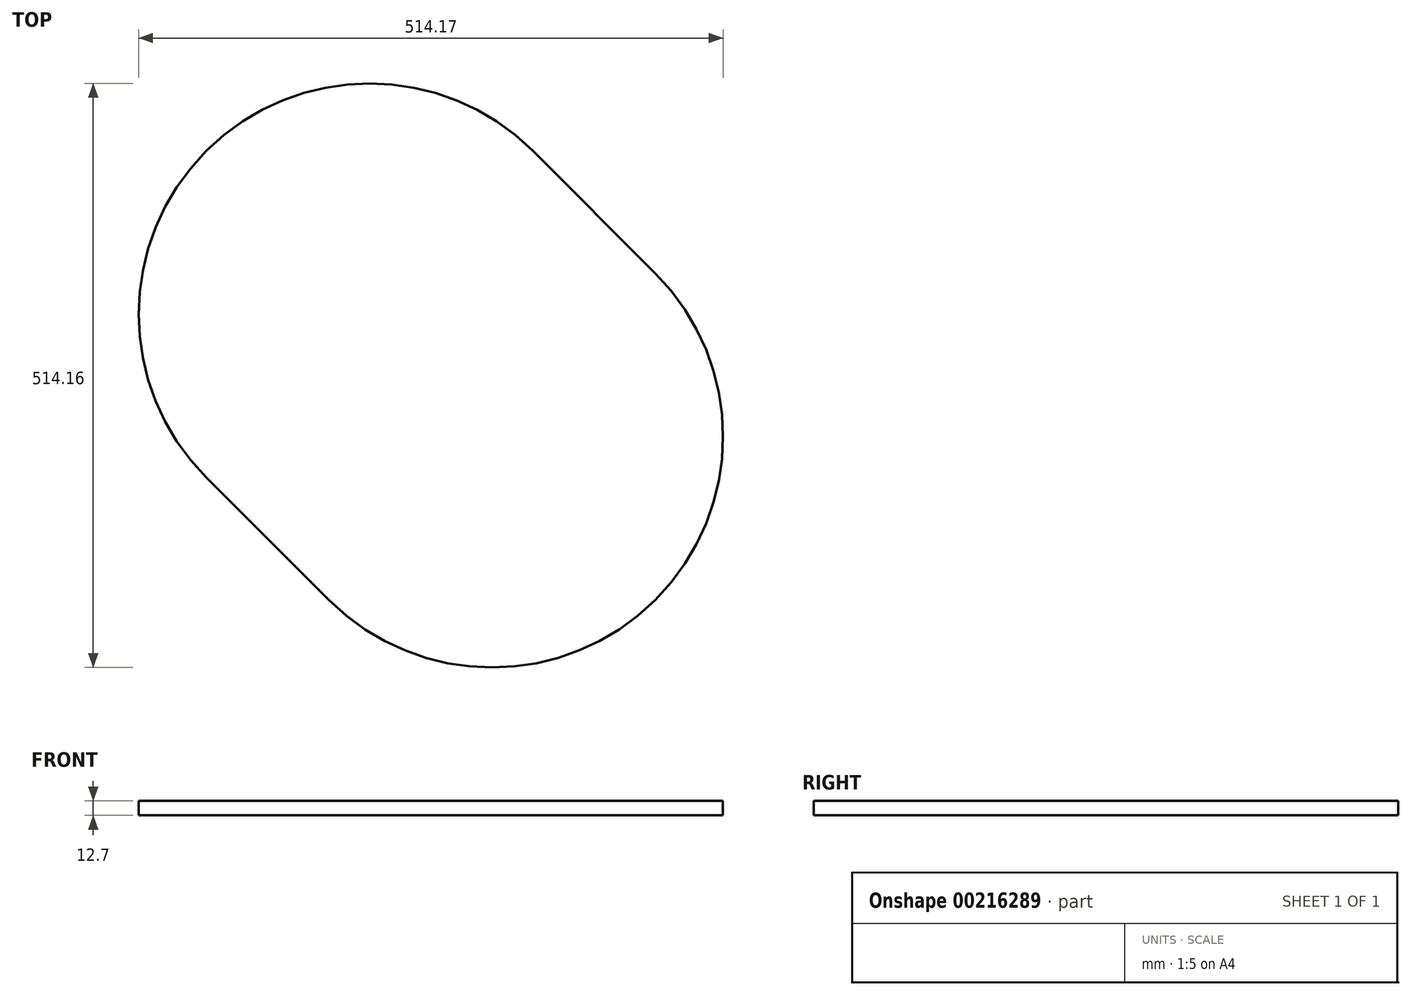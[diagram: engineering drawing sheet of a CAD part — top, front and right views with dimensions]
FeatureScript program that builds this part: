
annotation { "Feature Type Name" : "Feature", "Feature Type Description" : "" }
export const myFeature = defineFeature(function(context is Context, id is Id, definition is map)
    precondition{}
    {
        {
            var Q0;
            Q0=qCreatedBy(makeId("Top.planeOp"),FACE);
            var sketch = newSketch(context, id + "F0", { "sketchPlane" : qUnion([Q0])});
            skArc(sketch, "E0", {"start": v(-5251.06, 895.22) * mm, "mid": v(-5538.43, 895.22) * mm, "end": v(-5538.43, 607.85) * mm});
            skArc(sketch, "E1", {"start": v(-5430.67, 500.08) * mm, "mid": v(-5143.3, 500.08) * mm, "end": v(-5143.3, 787.45) * mm});
            skLineSegment(sketch, "E2", {"start": v(-5251.06, 895.22) * mm, "end": v(-5143.3, 787.45) * mm});
            skLineSegment(sketch, "E3", {"start": v(-5538.43, 607.85) * mm, "end": v(-5430.67, 500.08) * mm});
            skLineSegment(sketch, "E4", {"start": v(-8374.52, 1221.43) * mm, "end": v(-7345.82, 1221.43) * mm});
            skLineSegment(sketch, "E5", {"start": v(-7409.32, -1978.97) * mm, "end": v(-4869.32, -1978.97) * mm});
            skLineSegment(sketch, "E6", {"start": v(-7409.32, -1449.55) * mm, "end": v(-7409.32, -1978.97) * mm});
            skLineSegment(sketch, "E7", {"start": v(-7345.82, 980.13) * mm, "end": v(-8374.52, 980.13) * mm});
            skLineSegment(sketch, "E8", {"start": v(-8374.52, 992.83) * mm, "end": v(-8374.52, 1221.43) * mm});
            skLineSegment(sketch, "E9", {"start": v(-7345.82, 980.13) * mm, "end": v(-6723.52, 980.13) * mm});
            skLineSegment(sketch, "E10", {"start": v(-7345.82, 980.13) * mm, "end": v(-7345.82, 1221.43) * mm});
            skLineSegment(sketch, "E11", {"start": v(-5467.14, -705.4) * mm, "end": v(-5897.87, -225.9) * mm});
            skLineSegment(sketch, "E12", {"start": v(-4869.32, -1978.97) * mm, "end": v(-4869.32, 1221.43) * mm});
            skLineSegment(sketch, "E13", {"start": v(-7345.82, 1221.43) * mm, "end": v(-4869.32, 1221.43) * mm});
            skLineSegment(sketch, "E14", {"start": v(-7460.12, 281.63) * mm, "end": v(-6960.57, 281.63) * mm});
            skLineSegment(sketch, "E15", {"start": v(-5587.74, -1477.13) * mm, "end": v(-5472.75, -1362.15) * mm});
            skLineSegment(sketch, "E16", {"start": v(-5928.07, -1521.77) * mm, "end": v(-5695.5, -1521.77) * mm});
            skArc(sketch, "E17", {"start": v(-5695.5, -1521.77) * mm, "mid": v(-5637.18, -1510.17) * mm, "end": v(-5587.74, -1477.13) * mm});
            skLineSegment(sketch, "E18", {"start": v(-5428.12, -807.23) * mm, "end": v(-5428.12, -1254.38) * mm});
            skArc(sketch, "E19", {"start": v(-5428.12, -807.23) * mm, "mid": v(-5438.2, -752.7) * mm, "end": v(-5467.14, -705.4) * mm});
            skArc(sketch, "E20", {"start": v(-5472.75, -1362.15) * mm, "mid": v(-5439.72, -1312.7) * mm, "end": v(-5428.12, -1254.38) * mm});
            skLineSegment(sketch, "E21", {"start": v(-6822.36, 193.46) * mm, "end": v(-6066.27, -1433.6) * mm});
            skArc(sketch, "E22", {"start": v(-6066.27, -1433.6) * mm, "mid": v(-6010.04, -1497.85) * mm, "end": v(-5928.07, -1521.77) * mm});
            skArc(sketch, "E23", {"start": v(-6822.36, 193.46) * mm, "mid": v(-6878.6, 257.71) * mm, "end": v(-6960.57, 281.63) * mm});
            skLineSegment(sketch, "E24", {"start": v(-6113.92, 209.42) * mm, "end": v(-6113.92, 370.53) * mm});
            skLineSegment(sketch, "E25", {"start": v(-6099.72, 145.2) * mm, "end": v(-5997.2, -75.42) * mm});
            skArc(sketch, "E26", {"start": v(-6113.92, 209.42) * mm, "mid": v(-6110.33, 176.53) * mm, "end": v(-6099.72, 145.2) * mm});
            skArc(sketch, "E27", {"start": v(-5997.2, -75.42) * mm, "mid": v(-5953.13, -154.35) * mm, "end": v(-5897.87, -225.9) * mm});
            skArc(sketch, "E28", {"start": v(-6113.92, 370.53) * mm, "mid": v(-6292.46, 801.58) * mm, "end": v(-6723.52, 980.13) * mm});
            skLineSegment(sketch, "E29", {"start": v(-7612.52, -242.32) * mm, "end": v(-7612.52, 129.23) * mm});
            skArc(sketch, "E30", {"start": v(-7460.12, 281.63) * mm, "mid": v(-7567.88, 237) * mm, "end": v(-7612.52, 129.23) * mm});
            skLineSegment(sketch, "E31", {"start": v(-7411.52, -1423.72) * mm, "end": v(-7610.3, -268.16) * mm});
            skArc(sketch, "E32", {"start": v(-7409.32, -1449.55) * mm, "mid": v(-7409.87, -1436.59) * mm, "end": v(-7411.52, -1423.72) * mm});
            skArc(sketch, "E33", {"start": v(-7612.52, -242.32) * mm, "mid": v(-7611.96, -255.29) * mm, "end": v(-7610.3, -268.16) * mm});
            skLineSegment(sketch, "E34", {"start": v(-8374.52, 980.13) * mm, "end": v(-8374.52, 1221.43) * mm});
            skSolve(sketch);
        }
        {
            var Q0;
            Q0=makeQuery(id+"F0.imprint","IMPRINT",FACE,{"disambiguationData":[TD([[makeQuery(id+"F0.imprint","IMPRINT",EDGE,{"derivedFrom":sQuery(id+"F0.wireOp",EDGE,"E0")}),1.0]])]});
            extrude(context, id + "F1", {"entities" : qUnion([Q0]), "depth" : 12.7 * mm});
        }
    });
